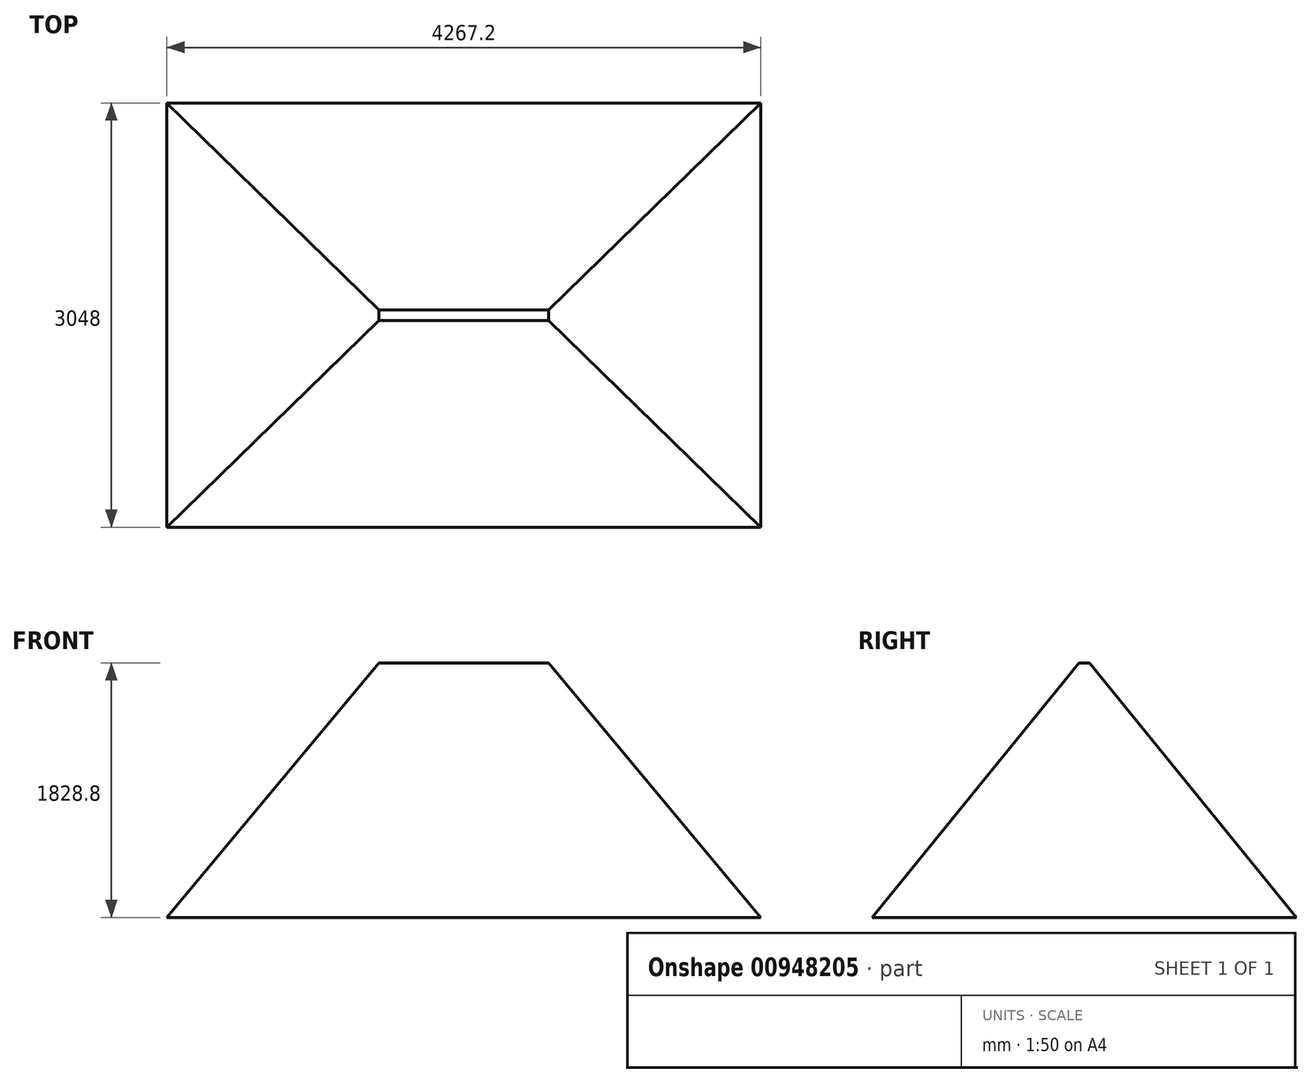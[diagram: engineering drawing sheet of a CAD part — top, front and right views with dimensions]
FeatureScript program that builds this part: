
annotation { "Feature Type Name" : "Feature", "Feature Type Description" : "" }
export const myFeature = defineFeature(function(context is Context, id is Id, definition is map)
    precondition{}
    {
        {
            var Q0;
            Q0=qCreatedBy(makeId("Top.planeOp"),FACE);
            var sketch = newSketch(context, id + "F0", { "sketchPlane" : qUnion([Q0])});
            skLineSegment(sketch, "E0.bottom", {"start": v(-2133.6, -1524) * mm, "end": v(2133.6, -1524) * mm});
            skLineSegment(sketch, "E0.top", {"start": v(-2133.6, 1524) * mm, "end": v(2133.6, 1524) * mm});
            skLineSegment(sketch, "E0.left", {"start": v(-2133.6, -1524) * mm, "end": v(-2133.6, 1524) * mm});
            skLineSegment(sketch, "E0.right", {"start": v(2133.6, -1524) * mm, "end": v(2133.6, 1524) * mm});
            skPoint(sketch, "E0.middle", {"position": v(0, 0) * mm});
            skSolve(sketch);
        }
        {
            var Q0;
            Q0=makeQuery(id+"F0.imprint","IMPRINT",FACE,{"disambiguationData":[TD([[makeQuery(id+"F0.imprint","IMPRINT",EDGE,{"derivedFrom":sQuery(id+"F0.wireOp",EDGE,"E0.bottom")}),1.0]])]});
            cPlane(context, id + "F1", {"entities" : qUnion([Q0]), "cplaneType" : CPlaneType.OFFSET, "offset" : 1828.8 * mm, "width" : 152.4 * mm, "height" : 152.4 * mm});
        }
        {
            var Q0;
            Q0=qCreatedBy(id+"F1.planeOp",FACE);
            var sketch = newSketch(context, id + "F2", { "sketchPlane" : qUnion([Q0])});
            skLineSegment(sketch, "E1.bottom", {"start": v(-609.6, -38.1) * mm, "end": v(609.6, -38.1) * mm});
            skLineSegment(sketch, "E1.top", {"start": v(-609.6, 38.1) * mm, "end": v(609.6, 38.1) * mm});
            skLineSegment(sketch, "E1.left", {"start": v(-609.6, -38.1) * mm, "end": v(-609.6, 38.1) * mm});
            skLineSegment(sketch, "E1.right", {"start": v(609.6, -38.1) * mm, "end": v(609.6, 38.1) * mm});
            skPoint(sketch, "E1.middle", {"position": v(0, 0) * mm});
            skSolve(sketch);
        }
        {
            var Q0;
            Q0=makeQuery(id+"F0.imprint","IMPRINT",FACE,{"disambiguationData":[TD([[makeQuery(id+"F0.imprint","IMPRINT",EDGE,{"derivedFrom":sQuery(id+"F0.wireOp",EDGE,"E0.bottom")}),1.0]])]});
            var Q1;
            Q1=makeQuery(id+"F2.imprint","IMPRINT",FACE,{"disambiguationData":[TD([[makeQuery(id+"F2.imprint","IMPRINT",EDGE,{"derivedFrom":sQuery(id+"F2.wireOp",EDGE,"E1.bottom")}),1.0]])]});
            loft(context, id + "F3", {"sheetProfilesArray" : [{ "sheetProfileEntities" : qUnion([Q0]) }, { "sheetProfileEntities" : qUnion([Q1]) }]});
        }
    });
